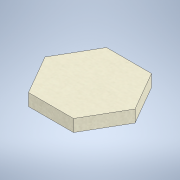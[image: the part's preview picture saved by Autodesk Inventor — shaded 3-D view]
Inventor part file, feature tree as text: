
AUTODESK INVENTOR PART (.ipt)
format: ipt  version: 2021 (Build 250183000, 183)  size: 103,424 bytes
history: native  units: mm
features: extrude x1, sketch x1
ambient origin geometry x8: Origin, YZ Plane, XZ Plane, XY Plane, X Axis, Y Axis, Z Axis, Center Point
bodies: Solid1 (feature_tree)
feature tree (2):
  extrude  "Extrusion1"  Depth=15.7mm TaperAngle=0.0deg
  sketch  "Sketch1"  dims[d0=101.0mm d1=15.7mm d2=0.0mm]
